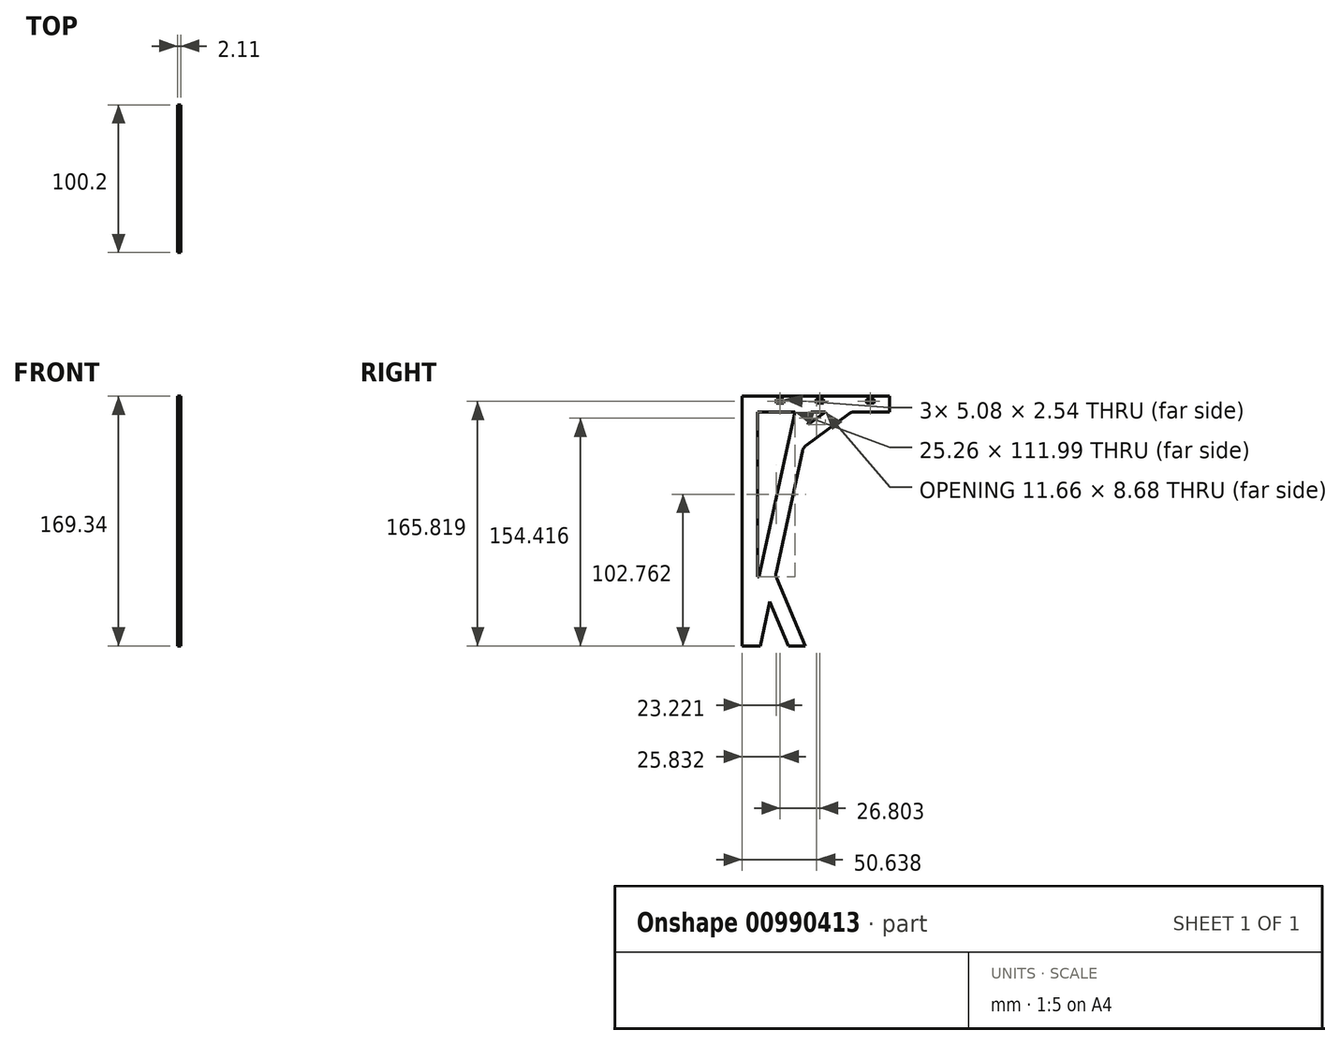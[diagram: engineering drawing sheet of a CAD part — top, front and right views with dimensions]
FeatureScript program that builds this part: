
annotation { "Feature Type Name" : "Feature", "Feature Type Description" : "" }
export const myFeature = defineFeature(function(context is Context, id is Id, definition is map)
    precondition{}
    {
        {
            var Q0;
            Q0=qCreatedBy(makeId("Right.planeOp"),FACE);
            var sketch = newSketch(context, id + "F0", { "sketchPlane" : qUnion([Q0])});
            skLineSegment(sketch, "E0", {"start": v(0, 0) * mm, "end": v(0, 169.34) * mm});
            skLineSegment(sketch, "E1", {"start": v(0, 169.34) * mm, "end": v(200.4, 169.34) * mm});
            skLineSegment(sketch, "E2", {"start": v(0, 0) * mm, "end": v(43.05, 0) * mm, "construction": true});
            skLineSegment(sketch, "E3", {"start": v(43.05, 0) * mm, "end": v(23.47, 45.96) * mm});
            skLineSegment(sketch, "E4", {"start": v(0, 47.82) * mm, "end": v(22.68, 47.82) * mm, "construction": true});
            skLineSegment(sketch, "E5", {"start": v(22.68, 47.82) * mm, "end": v(22.68, 0) * mm, "construction": true});
            skLineSegment(sketch, "E6", {"start": v(23.1, 49.8) * mm, "end": v(40.9, 132) * mm});
            skLineSegment(sketch, "E7", {"start": v(41.4, 134.33) * mm, "end": v(0, 134.33) * mm, "construction": true});
            skLineSegment(sketch, "E8", {"start": v(41.4, 134.33) * mm, "end": v(43.05, 0) * mm, "construction": true});
            skLineSegment(sketch, "E9", {"start": v(43.31, 135.75) * mm, "end": v(72.51, 157.5) * mm});
            skLineSegment(sketch, "E10", {"start": v(74.2, 158.76) * mm, "end": v(74.2, 169.34) * mm, "construction": true});
            skLineSegment(sketch, "E11", {"start": v(74.2, 158.76) * mm, "end": v(0, 158.76) * mm, "construction": true});
            skPoint(sketch, "E12", {"position": v(100.2, 169.34) * mm});
            skLineSegment(sketch, "E13", {"start": v(100.2, 169.34) * mm, "end": v(100.2, 154.3) * mm, "construction": true});
            skLineSegment(sketch, "E14", {"start": v(76.3, 158.76) * mm, "end": v(100.2, 158.76) * mm});
            skLineSegment(sketch, "E15.4", {"start": v(41.18, -0.8) * mm, "end": v(20.56, 47.62) * mm, "construction": true});
            skLineSegment(sketch, "E15.5", {"start": v(20.56, 47.62) * mm, "end": v(39.58, 135.5) * mm});
            skLineSegment(sketch, "E15.6", {"start": v(39.58, 135.5) * mm, "end": v(73.52, 160.79) * mm});
            skLineSegment(sketch, "E15.7", {"start": v(73.52, 160.79) * mm, "end": v(100.2, 160.79) * mm});
            skLineSegment(sketch, "E16.5", {"start": v(11.62, 46.77) * mm, "end": v(31.89, 140.45) * mm});
            skLineSegment(sketch, "E16.6", {"start": v(31.89, 140.45) * mm, "end": v(70.69, 169.35) * mm, "construction": true});
            skLineSegment(sketch, "E16.7", {"start": v(70.69, 169.35) * mm, "end": v(100.2, 169.35) * mm});
            skLineSegment(sketch, "E17", {"start": v(31.89, 140.45) * mm, "end": v(38.14, 169.34) * mm, "construction": true});
            skLineSegment(sketch, "E18", {"start": v(10.6, 158.76) * mm, "end": v(0, 158.76) * mm, "construction": true});
            skLineSegment(sketch, "E19", {"start": v(10.6, 158.76) * mm, "end": v(10.6, 46.77) * mm});
            skLineSegment(sketch, "E20", {"start": v(10.6, 46.77) * mm, "end": v(11.62, 46.77) * mm});
            skLineSegment(sketch, "E21", {"start": v(36.3, 160.79) * mm, "end": v(31.89, 140.45) * mm, "construction": true});
            skLineSegment(sketch, "E22", {"start": v(41.4, 134.33) * mm, "end": v(48.98, 169.34) * mm, "construction": true});
            skLineSegment(sketch, "E23", {"start": v(47.13, 160.79) * mm, "end": v(44.8, 150.07) * mm});
            skLineSegment(sketch, "E24", {"start": v(13.2, 0) * mm, "end": v(0, 0) * mm});
            skLineSegment(sketch, "E25", {"start": v(31.54, 0) * mm, "end": v(43.05, 0) * mm});
            skLineSegment(sketch, "E26", {"start": v(100.2, 158.76) * mm, "end": v(100.2, 169.35) * mm});
            skPoint(sketch, "E27", {"position": v(46.69, 158.76) * mm});
            skPoint(sketch, "E28", {"position": v(56.47, 158.76) * mm});
            skLineSegment(sketch, "E29", {"start": v(46.69, 158.76) * mm, "end": v(56.47, 158.76) * mm});
            skLineSegment(sketch, "E30", {"start": v(44.8, 150.07) * mm, "end": v(46.69, 158.76) * mm});
            skLineSegment(sketch, "E31", {"start": v(10.6, 158.76) * mm, "end": v(35.85, 158.76) * mm});
            skLineSegment(sketch, "E32", {"start": v(35.85, 158.76) * mm, "end": v(31.89, 140.45) * mm});
            skLineSegment(sketch, "E33", {"start": v(44.8, 150.07) * mm, "end": v(56.47, 158.76) * mm});
            skLineSegment(sketch, "E34", {"start": v(30.88, 85.7) * mm, "end": v(20.53, 87.94) * mm, "construction": true});
            skLineSegment(sketch, "E35.0", {"start": v(33.3, -4.15) * mm, "end": v(12.94, 43.67) * mm, "construction": true});
            skLineSegment(sketch, "E36", {"start": v(22.68, 47.82) * mm, "end": v(18.8, 29.9) * mm, "construction": true});
            skLineSegment(sketch, "E37", {"start": v(18.8, 29.9) * mm, "end": v(12.34, 0) * mm});
            skLineSegment(sketch, "E38", {"start": v(18.8, 29.9) * mm, "end": v(31.54, 0) * mm});
            skLineSegment(sketch, "E39", {"start": v(12.34, 0) * mm, "end": v(31.54, 0) * mm});
            skLineSegment(sketch, "E40", {"start": v(20.56, 47.62) * mm, "end": v(40.84, 0) * mm});
            skPoint(sketch, "E41.visualSharp", {"position": v(41.4, 134.33) * mm});
            skArc(sketch, "E41.filletArc", {"start": v(43.31, 135.75) * mm, "mid": v(41.77, 134.1) * mm, "end": v(40.9, 132) * mm});
            skPoint(sketch, "E42.visualSharp", {"position": v(22.68, 47.82) * mm});
            skArc(sketch, "E42.filletArc", {"start": v(23.1, 49.8) * mm, "mid": v(23, 47.85) * mm, "end": v(23.47, 45.96) * mm});
            skPoint(sketch, "E43.visualSharp", {"position": v(74.2, 158.76) * mm});
            skArc(sketch, "E43.filletArc", {"start": v(76.3, 158.76) * mm, "mid": v(74.3, 158.44) * mm, "end": v(72.51, 157.5) * mm});
            skPoint(sketch, "E44", {"position": v(21.75, 93.6) * mm});
            skLineSegment(sketch, "E45", {"start": v(21.75, 93.6) * mm, "end": v(22.1, 95.21) * mm});
            skLineSegment(sketch, "E46", {"start": v(22.1, 95.21) * mm, "end": v(26.54, 94.25) * mm});
            skLineSegment(sketch, "E47", {"start": v(29.56, 96.2) * mm, "end": v(37.5, 132.86) * mm});
            skLineSegment(sketch, "E48", {"start": v(35.55, 135.88) * mm, "end": v(31.1, 136.84) * mm});
            skPoint(sketch, "E49.visualSharp", {"position": v(38.03, 135.35) * mm});
            skArc(sketch, "E49.filletArc", {"start": v(37.5, 132.86) * mm, "mid": v(37.15, 134.78) * mm, "end": v(35.55, 135.88) * mm});
            skPoint(sketch, "E50.visualSharp", {"position": v(29.02, 93.72) * mm});
            skArc(sketch, "E50.filletArc", {"start": v(26.54, 94.25) * mm, "mid": v(28.45, 94.6) * mm, "end": v(29.56, 96.2) * mm});
            skLineSegment(sketch, "E51", {"start": v(21.75, 93.6) * mm, "end": v(32.1, 91.37) * mm, "construction": true});
            skLineSegment(sketch, "E52.0", {"start": v(35.01, 133.4) * mm, "end": v(30.57, 134.36) * mm});
            skLineSegment(sketch, "E52.1", {"start": v(22.64, 97.7) * mm, "end": v(27.08, 96.74) * mm});
            skLineSegment(sketch, "E52.2", {"start": v(27.08, 96.74) * mm, "end": v(27.08, 96.74) * mm});
            skLineSegment(sketch, "E52.3", {"start": v(27.08, 96.74) * mm, "end": v(35.01, 133.4) * mm});
            skLineSegment(sketch, "E52.4", {"start": v(35.01, 133.4) * mm, "end": v(35.01, 133.4) * mm});
            skLineSegment(sketch, "E53.MirrorCS", {"start": v(21.4, 92) * mm, "end": v(25.85, 91.04) * mm});
            skArc(sketch, "E54.MirrorCS", {"start": v(25.85, 91.04) * mm, "mid": v(27.44, 89.94) * mm, "end": v(27.8, 88.02) * mm});
            skLineSegment(sketch, "E55.MirrorCS", {"start": v(27.8, 88.02) * mm, "end": v(19.86, 51.36) * mm});
            skArc(sketch, "E56.MirrorCS", {"start": v(19.86, 51.36) * mm, "mid": v(18.75, 49.76) * mm, "end": v(16.84, 49.41) * mm});
            skLineSegment(sketch, "E57.MirrorCS", {"start": v(16.84, 49.41) * mm, "end": v(12.4, 50.38) * mm});
            skLineSegment(sketch, "E58.MirrorCS", {"start": v(17.37, 51.9) * mm, "end": v(12.94, 52.86) * mm});
            skLineSegment(sketch, "E59.MirrorCS", {"start": v(25.3, 88.56) * mm, "end": v(17.37, 51.9) * mm});
            skLineSegment(sketch, "E60.MirrorCS", {"start": v(20.87, 89.52) * mm, "end": v(25.3, 88.56) * mm});
            skLineSegment(sketch, "E61", {"start": v(33.72, 127.42) * mm, "end": v(31.23, 127.96) * mm});
            skLineSegment(sketch, "E62", {"start": v(31.23, 127.96) * mm, "end": v(30.16, 123) * mm});
            skLineSegment(sketch, "E63", {"start": v(30.16, 123) * mm, "end": v(32.64, 122.46) * mm});
            skLineSegment(sketch, "E64", {"start": v(28.37, 102.7) * mm, "end": v(25.88, 103.24) * mm});
            skLineSegment(sketch, "E65", {"start": v(25.88, 103.24) * mm, "end": v(26.96, 108.2) * mm});
            skLineSegment(sketch, "E66", {"start": v(26.96, 108.2) * mm, "end": v(29.44, 107.66) * mm});
            skLineSegment(sketch, "E67.MirrorCS", {"start": v(24.02, 82.6) * mm, "end": v(21.54, 83.13) * mm});
            skLineSegment(sketch, "E68.MirrorCS", {"start": v(21.54, 83.13) * mm, "end": v(20.46, 78.17) * mm});
            skLineSegment(sketch, "E69.MirrorCS", {"start": v(20.46, 78.17) * mm, "end": v(22.94, 77.63) * mm});
            skLineSegment(sketch, "E70.MirrorCS", {"start": v(17.26, 63.37) * mm, "end": v(19.74, 62.84) * mm});
            skLineSegment(sketch, "E71.MirrorCS", {"start": v(16.19, 58.4) * mm, "end": v(17.26, 63.37) * mm});
            skLineSegment(sketch, "E72.MirrorCS", {"start": v(18.67, 57.87) * mm, "end": v(16.19, 58.4) * mm});
            skLineSegment(sketch, "E73", {"start": v(31.89, 140.45) * mm, "end": v(41.4, 134.33) * mm, "construction": true});
            skLineSegment(sketch, "E74.MirrorCS", {"start": v(37.56, 139.02) * mm, "end": v(34.85, 142.66) * mm});
            skArc(sketch, "E75.MirrorCS", {"start": v(41.12, 138.5) * mm, "mid": v(39.23, 138.02) * mm, "end": v(37.56, 139.02) * mm});
            skLineSegment(sketch, "E76.MirrorCS", {"start": v(71.2, 160.9) * mm, "end": v(41.12, 138.5) * mm});
            skArc(sketch, "E77.MirrorCS", {"start": v(71.72, 164.46) * mm, "mid": v(72.2, 162.57) * mm, "end": v(71.2, 160.9) * mm});
            skLineSegment(sketch, "E78.MirrorCS", {"start": v(69, 168.1) * mm, "end": v(71.72, 164.46) * mm});
            skLineSegment(sketch, "E79.MirrorCS", {"start": v(66.97, 166.58) * mm, "end": v(69.69, 162.94) * mm});
            skLineSegment(sketch, "E80.MirrorCS", {"start": v(69.69, 162.94) * mm, "end": v(39.6, 140.53) * mm});
            skLineSegment(sketch, "E81.MirrorCS", {"start": v(64.8, 159.3) * mm, "end": v(63.28, 161.33) * mm});
            skLineSegment(sketch, "E82.MirrorCS", {"start": v(63.28, 161.33) * mm, "end": v(59.2, 158.3) * mm});
            skLineSegment(sketch, "E83.MirrorCS", {"start": v(59.2, 158.3) * mm, "end": v(60.72, 156.26) * mm});
            skLineSegment(sketch, "E84.MirrorCS", {"start": v(47.06, 149.26) * mm, "end": v(48.58, 147.22) * mm});
            skLineSegment(sketch, "E85.MirrorCS", {"start": v(42.99, 146.22) * mm, "end": v(47.06, 149.26) * mm});
            skLineSegment(sketch, "E86.MirrorCS", {"start": v(44.5, 144.19) * mm, "end": v(42.99, 146.22) * mm});
            skLineSegment(sketch, "E87.MirrorCS", {"start": v(39.6, 140.53) * mm, "end": v(36.89, 144.18) * mm});
            skLineSegment(sketch, "E88", {"start": v(70.69, 169.35) * mm, "end": v(70.69, 164.55) * mm});
            skPoint(sketch, "E89.visualSharp", {"position": v(70.69, 162) * mm});
            skArc(sketch, "E89.filletArc", {"start": v(68.15, 162) * mm, "mid": v(69.94, 162.75) * mm, "end": v(70.69, 164.55) * mm});
            skLineSegment(sketch, "E90.1", {"start": v(68.15, 169.63) * mm, "end": v(68.15, 164.55) * mm});
            skLineSegment(sketch, "E91", {"start": v(55.17, 164.55) * mm, "end": v(55.17, 167.09) * mm});
            skLineSegment(sketch, "E92", {"start": v(55.17, 167.09) * mm, "end": v(50.1, 167.09) * mm});
            skLineSegment(sketch, "E93", {"start": v(50.1, 167.09) * mm, "end": v(50.1, 164.55) * mm});
            skLineSegment(sketch, "E94", {"start": v(28.37, 164.55) * mm, "end": v(28.37, 167.09) * mm});
            skLineSegment(sketch, "E95", {"start": v(28.37, 167.09) * mm, "end": v(23.3, 167.09) * mm});
            skLineSegment(sketch, "E96", {"start": v(23.3, 167.09) * mm, "end": v(23.3, 164.55) * mm});
            skLineSegment(sketch, "E97", {"start": v(22.68, 47.82) * mm, "end": v(11.62, 46.77) * mm, "construction": true});
            skLineSegment(sketch, "E98", {"start": v(15.36, 37.97) * mm, "end": v(19.78, 39.85) * mm});
            skLineSegment(sketch, "E99", {"start": v(23.11, 38.51) * mm, "end": v(37.3, 5.2) * mm});
            skLineSegment(sketch, "E100", {"start": v(35.96, 1.87) * mm, "end": v(31.54, -0.01) * mm});
            skPoint(sketch, "E101.visualSharp", {"position": v(38.3, 2.87) * mm});
            skArc(sketch, "E101.filletArc", {"start": v(35.96, 1.87) * mm, "mid": v(37.32, 3.26) * mm, "end": v(37.3, 5.2) * mm});
            skPoint(sketch, "E102.visualSharp", {"position": v(22.12, 40.85) * mm});
            skArc(sketch, "E102.filletArc", {"start": v(23.11, 38.51) * mm, "mid": v(21.72, 39.87) * mm, "end": v(19.78, 39.85) * mm});
            skLineSegment(sketch, "E103.0", {"start": v(34.97, 4.2) * mm, "end": v(25.52, 0.18) * mm});
            skLineSegment(sketch, "E103.1", {"start": v(20.78, 37.52) * mm, "end": v(34.97, 4.2) * mm});
            skLineSegment(sketch, "E103.2", {"start": v(16.36, 35.63) * mm, "end": v(20.78, 37.52) * mm});
            skLineSegment(sketch, "E104", {"start": v(27.86, 20.9) * mm, "end": v(25.52, 19.9) * mm});
            skLineSegment(sketch, "E105", {"start": v(25.52, 19.9) * mm, "end": v(23.53, 24.57) * mm});
            skLineSegment(sketch, "E106", {"start": v(23.53, 24.57) * mm, "end": v(25.87, 25.57) * mm});
            skLineSegment(sketch, "E107", {"start": v(21.48, 35.85) * mm, "end": v(19.15, 34.86) * mm});
            skLineSegment(sketch, "E108", {"start": v(19.15, 34.86) * mm, "end": v(21.14, 30.18) * mm});
            skLineSegment(sketch, "E109", {"start": v(21.14, 30.18) * mm, "end": v(23.48, 31.18) * mm});
            skLineSegment(sketch, "E110", {"start": v(79.6, 169.35) * mm, "end": v(79.6, 164.55) * mm});
            skLineSegment(sketch, "E111", {"start": v(82.14, 162) * mm, "end": v(100.2, 162) * mm});
            skPoint(sketch, "E112.visualSharp", {"position": v(79.6, 162) * mm});
            skArc(sketch, "E112.filletArc", {"start": v(79.6, 164.55) * mm, "mid": v(80.34, 162.75) * mm, "end": v(82.14, 162) * mm});
            skLineSegment(sketch, "E113.0", {"start": v(82.14, 164.55) * mm, "end": v(100.2, 164.55) * mm});
            skLineSegment(sketch, "E113.1", {"start": v(82.14, 169.35) * mm, "end": v(82.14, 164.55) * mm});
            skLineSegment(sketch, "E114", {"start": v(84.57, 164.55) * mm, "end": v(84.57, 167.09) * mm});
            skPoint(sketch, "E114.endSnap0", {"position": v(68.15, 167.09) * mm});
            skLineSegment(sketch, "E115", {"start": v(84.57, 167.09) * mm, "end": v(89.65, 167.09) * mm});
            skLineSegment(sketch, "E116", {"start": v(89.65, 167.09) * mm, "end": v(89.65, 164.55) * mm});
            skLineSegment(sketch, "E117", {"start": v(10.6, 158.76) * mm, "end": v(10.6, 164.55) * mm, "construction": true});
            skLineSegment(sketch, "E118", {"start": v(68.15, 164.55) * mm, "end": v(18.21, 164.55) * mm});
            skLineSegment(sketch, "E119", {"start": v(68.15, 162) * mm, "end": v(18.21, 162) * mm});
            skLineSegment(sketch, "E120", {"start": v(18.21, 164.55) * mm, "end": v(18.21, 169.34) * mm});
            skLineSegment(sketch, "E121", {"start": v(15.67, 164.55) * mm, "end": v(15.67, 169.34) * mm});
            skPoint(sketch, "E122.visualSharp", {"position": v(15.67, 162) * mm});
            skArc(sketch, "E122.filletArc", {"start": v(15.67, 164.55) * mm, "mid": v(16.42, 162.75) * mm, "end": v(18.21, 162) * mm});
            skLineSegment(sketch, "E123", {"start": v(15.67, 164.55) * mm, "end": v(18.21, 164.55) * mm, "construction": true});
            skLineSegment(sketch, "E124", {"start": v(10.6, 164.55) * mm, "end": v(15.67, 164.55) * mm, "construction": true});
            skLineSegment(sketch, "E125", {"start": v(23.3, 165.82) * mm, "end": v(18.21, 165.82) * mm, "construction": true});
            skSolve(sketch);
        }
        {
            var Q0;
            Q0=makeQuery(id+"F0.imprint","IMPRINT",FACE,{"disambiguationData":[TD([[makeQuery(id+"F0.imprint","IMPRINT",EDGE,{"derivedFrom":sQuery(id+"F0.wireOp",EDGE,"E15.5")}),1.0]])]});
            var Q1;
            {var subQ0=sQuery(id+"F0.wireOp",EDGE,"E91");Q1=makeQuery(id+"F0.imprint","IMPRINT",FACE,{"disambiguationData":[TD([[makeQuery(id+"F0.imprint","IMPRINT",EDGE,{"derivedFrom":subQ0}),-1.0]])]});}
            var Q2;
            {var subQ10=sQuery(id+"F0.wireOp",EDGE,"Y5XbKFPJ-2wYX-9icL-y4mU-RIpAKNCXkipD");Q2=makeQuery(id+"F0.imprint","IMPRINT",FACE,{"disambiguationData":[TD([[makeQuery(id+"F0.imprint","IMPRINT",EDGE,{"derivedFrom":subQ10}),-1.0]])]});}
            var Q3;
            {var subQ0=sQuery(id+"F0.wireOp",EDGE,"E84.MirrorCS");Q3=makeQuery(id+"F0.imprint","IMPRINT",FACE,{"disambiguationData":[TD([[makeQuery(id+"F0.imprint","IMPRINT",EDGE,{"derivedFrom":subQ0}),-1.0]])]});}
            var Q4;
            {var subQ0=sQuery(id+"F0.wireOp",EDGE,"E81.MirrorCS");Q4=makeQuery(id+"F0.imprint","IMPRINT",FACE,{"disambiguationData":[TD([[makeQuery(id+"F0.imprint","IMPRINT",EDGE,{"derivedFrom":subQ0}),1.0]])]});}
            var Q5;
            {var subQ0=sQuery(id+"F0.wireOp",EDGE,"E88");var subQ1=makeQuery(id+"F0.imprint","IMPRINT",VERTEX,{"derivedFrom":subQ0});Q5=makeQuery(id+"F0.imprint","IMPRINT",FACE,{"disambiguationData":[TD([[makeQuery(id+"F0.imprint","IMPRINT",EDGE,{"disambiguationData":[TD([[subQ1,1.0]])],"derivedFrom":subQ0}),-1.0]])]});}
            var Q6;
            {var subQ3=sQuery(id+"F0.wireOp",EDGE,"E114");Q6=makeQuery(id+"F0.imprint","IMPRINT",FACE,{"disambiguationData":[TD([[makeQuery(id+"F0.imprint","IMPRINT",EDGE,{"derivedFrom":subQ3}),1.0]])]});}
            var Q7;
            {var subQ4=sQuery(id+"F0.wireOp",EDGE,"E111");Q7=makeQuery(id+"F0.imprint","IMPRINT",FACE,{"disambiguationData":[TD([[makeQuery(id+"F0.imprint","IMPRINT",EDGE,{"derivedFrom":subQ4}),1.0]])]});}
            var Q8;
            {var subQ2=sQuery(id+"F0.wireOp",EDGE,"E3");Q8=makeQuery(id+"F0.imprint","IMPRINT",FACE,{"disambiguationData":[TD([[makeQuery(id+"F0.imprint","IMPRINT",EDGE,{"derivedFrom":subQ2}),1.0]])]});}
            var Q9;
            {var subQ5=sQuery(id+"F0.wireOp",EDGE,"E46");Q9=makeQuery(id+"F0.imprint","IMPRINT",FACE,{"disambiguationData":[TD([[makeQuery(id+"F0.imprint","IMPRINT",EDGE,{"derivedFrom":subQ5}),1.0]])]});}
            var Q10;
            {var subQ3=sQuery(id+"F0.wireOp",EDGE,"E52.0");Q10=makeQuery(id+"F0.imprint","IMPRINT",FACE,{"disambiguationData":[TD([[makeQuery(id+"F0.imprint","IMPRINT",EDGE,{"derivedFrom":subQ3}),1.0]])]});}
            var Q11;
            {var subQ0=sQuery(id+"F0.wireOp",EDGE,"E61");Q11=makeQuery(id+"F0.imprint","IMPRINT",FACE,{"disambiguationData":[TD([[makeQuery(id+"F0.imprint","IMPRINT",EDGE,{"derivedFrom":subQ0}),1.0]])]});}
            var Q12;
            {var subQ0=sQuery(id+"F0.wireOp",EDGE,"E64");Q12=makeQuery(id+"F0.imprint","IMPRINT",FACE,{"disambiguationData":[TD([[makeQuery(id+"F0.imprint","IMPRINT",EDGE,{"derivedFrom":subQ0}),-1.0]])]});}
            var Q13;
            {var subQ7=sQuery(id+"F0.wireOp",EDGE,"E53.MirrorCS");Q13=makeQuery(id+"F0.imprint","IMPRINT",FACE,{"disambiguationData":[TD([[makeQuery(id+"F0.imprint","IMPRINT",EDGE,{"derivedFrom":subQ7}),-1.0]])]});}
            var Q14;
            {var subQ0=sQuery(id+"F0.wireOp",EDGE,"E67.MirrorCS");Q14=makeQuery(id+"F0.imprint","IMPRINT",FACE,{"disambiguationData":[TD([[makeQuery(id+"F0.imprint","IMPRINT",EDGE,{"derivedFrom":subQ0}),1.0]])]});}
            var Q15;
            {var subQ4=sQuery(id+"F0.wireOp",EDGE,"E58.MirrorCS");Q15=makeQuery(id+"F0.imprint","IMPRINT",FACE,{"disambiguationData":[TD([[makeQuery(id+"F0.imprint","IMPRINT",EDGE,{"derivedFrom":subQ4}),-1.0]])]});}
            var Q16;
            {var subQ0=sQuery(id+"F0.wireOp",EDGE,"E70.MirrorCS");Q16=makeQuery(id+"F0.imprint","IMPRINT",FACE,{"disambiguationData":[TD([[makeQuery(id+"F0.imprint","IMPRINT",EDGE,{"derivedFrom":subQ0}),-1.0]])]});}
            var Q17;
            {var subQ0=sQuery(id+"F0.wireOp",EDGE,"E107");Q17=makeQuery(id+"F0.imprint","IMPRINT",FACE,{"disambiguationData":[TD([[makeQuery(id+"F0.imprint","IMPRINT",EDGE,{"derivedFrom":subQ0}),1.0]])]});}
            var Q18;
            {var subQ0=sQuery(id+"F0.wireOp",EDGE,"E104");Q18=makeQuery(id+"F0.imprint","IMPRINT",FACE,{"disambiguationData":[TD([[makeQuery(id+"F0.imprint","IMPRINT",EDGE,{"derivedFrom":subQ0}),-1.0]])]});}
            var Q19;
            {var subQ16=sQuery(id+"F0.wireOp",EDGE,"E119");Q19=makeQuery(id+"F0.imprint","IMPRINT",FACE,{"disambiguationData":[TD([[makeQuery(id+"F0.imprint","IMPRINT",EDGE,{"derivedFrom":subQ16}),-1.0]])]});}
            extrude(context, id + "F1", {"entities" : qUnion([Q0, Q1, Q2, Q3, Q4, Q5, Q6, Q7, Q8, Q9, Q10, Q11, Q12, Q13, Q14, Q15, Q16, Q17, Q18, Q19]), "depth" : 2.1 * mm, "offsetDistance" : 25.4 * mm});
        }
        {
            var Q0;
            Q0=makeQuery(id+"F1.opExtrude","CAP_EDGE",EDGE,{"disambiguationData":[OSD([sQuery(id+"F0.wireOp",EDGE,"E6")])],"isStart":true});
            fillet(context, id + "F2", {"entities" : qUnion([Q0]), "radius" : 0.76 * mm, "tangentPropagation" : true, "allowEdgeOverflow" : false});
        }
    });
